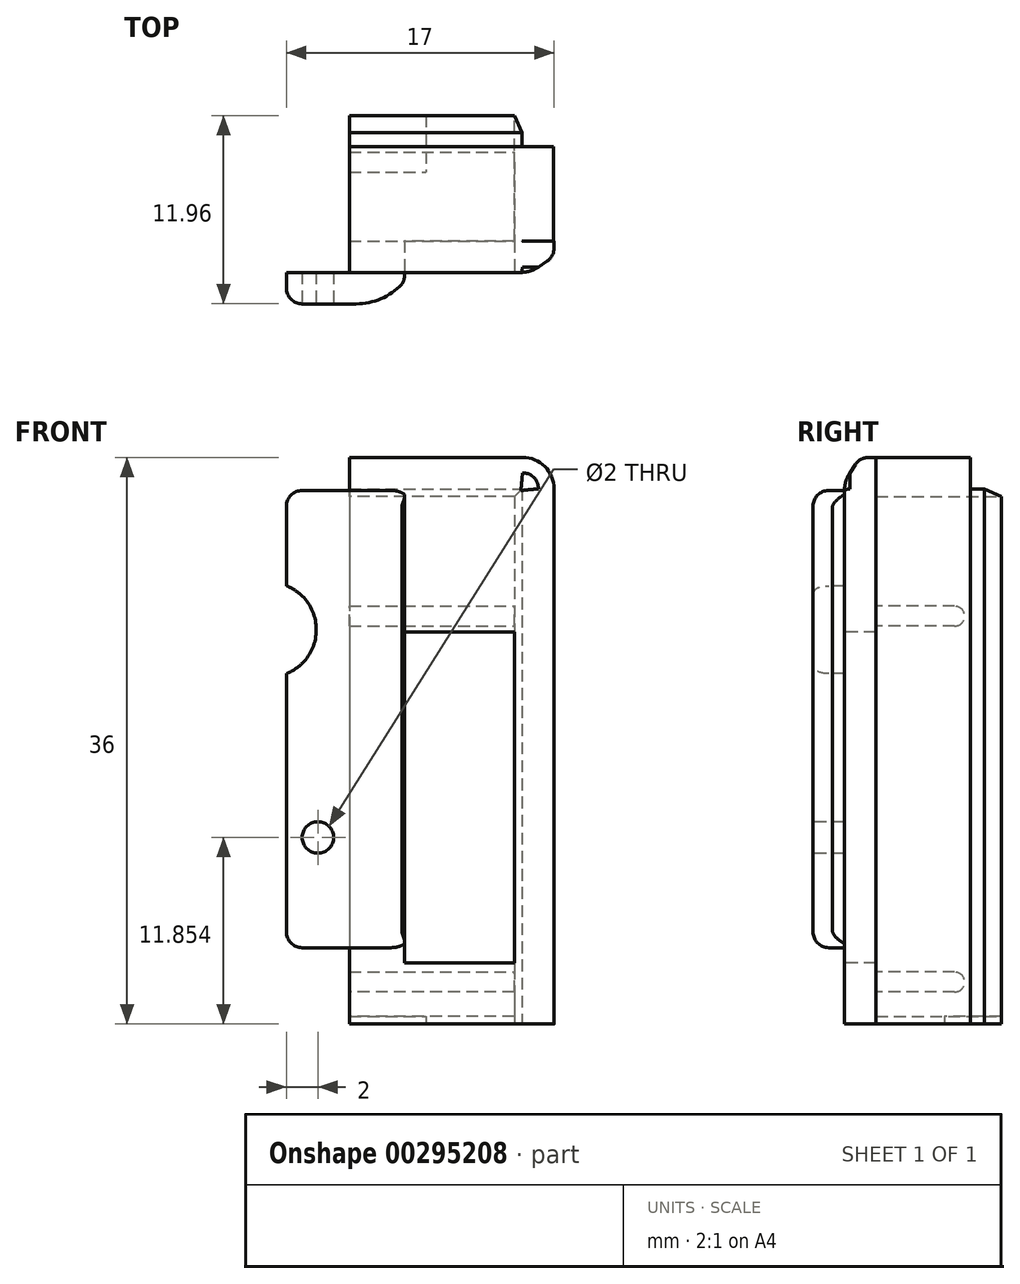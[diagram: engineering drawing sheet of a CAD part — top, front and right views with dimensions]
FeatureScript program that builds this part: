
annotation { "Feature Type Name" : "Feature", "Feature Type Description" : "" }
export const myFeature = defineFeature(function(context is Context, id is Id, definition is map)
    precondition{}
    {
        {
            var Q0;
            Q0=qCreatedBy(makeId("Front.planeOp"),FACE);
            var sketch = newSketch(context, id + "F0", { "sketchPlane" : qUnion([Q0])});
            skLineSegment(sketch, "E0", {"start": v(12.98, 36.3) * mm, "end": v(12.98, 70.29) * mm});
            skLineSegment(sketch, "E1", {"start": v(10.98, 72.29) * mm, "end": v(0, 72.29) * mm});
            skLineSegment(sketch, "E2", {"start": v(0, 72.29) * mm, "end": v(0, 70.29) * mm});
            skLineSegment(sketch, "E3", {"start": v(0, 70.29) * mm, "end": v(10.98, 70.29) * mm});
            skLineSegment(sketch, "E4", {"start": v(10.98, 70.29) * mm, "end": v(10.98, 36.3) * mm});
            skPoint(sketch, "E5.visualSharp", {"position": v(12.98, 72.29) * mm});
            skArc(sketch, "E5.filletArc", {"start": v(12.98, 70.29) * mm, "mid": v(12.4, 71.7) * mm, "end": v(10.98, 72.29) * mm});
            skPoint(sketch, "E6.visualSharp", {"position": v(12.98, 0) * mm});
            skLineSegment(sketch, "E7", {"start": v(10.98, 36.3) * mm, "end": v(12.98, 36.3) * mm});
            skPoint(sketch, "E8.start.orphan", {"position": v(0, 2) * mm});
            skSolve(sketch);
        }
        {
            var Q0;
            Q0=makeQuery(id+"F0.imprint","IMPRINT",FACE,{"disambiguationData":[TD([[makeQuery(id+"F0.imprint","IMPRINT",EDGE,{"derivedFrom":sQuery(id+"F0.wireOp",EDGE,"E0")}),1.0]])]});
            extrude(context, id + "F1", {"entities" : qUnion([Q0]), "depth" : 6 * mm});
        }
        {
            var Q0;
            Q0=makeQuery(id+"F1.opExtrude","SWEPT_FACE",FACE,{"disambiguationData":[OSD([sQuery(id+"F0.wireOp",EDGE,"E2")])]});
            var sketch = newSketch(context, id + "F2", { "sketchPlane" : qUnion([Q0])});
            skLineSegment(sketch, "E9.bottom", {"start": v(6, 72.29) * mm, "end": v(8, 72.29) * mm});
            skLineSegment(sketch, "E9.top", {"start": v(6, 36.3) * mm, "end": v(8, 36.3) * mm});
            skLineSegment(sketch, "E9.left", {"start": v(6, 72.29) * mm, "end": v(6, 36.3) * mm});
            skLineSegment(sketch, "E9.right", {"start": v(8, 72.29) * mm, "end": v(8, 36.3) * mm});
            skSolve(sketch);
        }
        {
            var Q0;
            Q0 = qSketchRegion(id + "F2", true);
            extrude(context, id + "F3", {"entities" : qUnion([Q0]), "operationType" : NewBodyOperationType.ADD, "oppositeDirection" : true, "depth" : 13 * mm});
        }
        {
            var Q0;
            Q0=makeQuery(id+"F3.opExtrude","CAP_EDGE",EDGE,{"disambiguationData":[OSD([sQuery(id+"F2.wireOp",EDGE,"E9.bottom")])],"isStart":false});
            fillet(context, id + "F4", {"entities" : qUnion([Q0]), "radius" : 2 * mm, "tangentPropagation" : true, "allowEdgeOverflow" : false});
        }
        {
            var Q0;
            Q0=makeQuery(id+"F3.opExtrude","SWEPT_FACE",FACE,{"disambiguationData":[OSD([sQuery(id+"F2.wireOp",EDGE,"E9.right")])]});
            var sketch = newSketch(context, id + "F5", { "sketchPlane" : qUnion([Q0])});
            skLineSegment(sketch, "E10.bottom", {"start": v(3.5, 70.18) * mm, "end": v(-4, 70.18) * mm});
            skLineSegment(sketch, "E10.top", {"start": v(3.5, 41.14) * mm, "end": v(-4, 41.14) * mm});
            skLineSegment(sketch, "E10.left", {"start": v(3.5, 70.18) * mm, "end": v(3.5, 41.14) * mm});
            skLineSegment(sketch, "E10.right", {"start": v(-4, 70.18) * mm, "end": v(-4, 41.14) * mm});
            skSolve(sketch);
        }
        {
            var Q0;
            Q0 = qSketchRegion(id + "F5", true);
            extrude(context, id + "F6", {"entities" : qUnion([Q0]), "operationType" : NewBodyOperationType.ADD, "depth" : 2 * mm});
        }
        {
            var Q0;
            Q0=makeQuery(id+"F6.opExtrude","CAP_EDGE",EDGE,{"disambiguationData":[OSD([sQuery(id+"F5.wireOp",EDGE,"E10.left")])],"isStart":false});
            chamfer(context, id + "F7", {"entities" : qUnion([Q0]), "chamferType" : ChamferType.TWO_OFFSETS, "width1" : 1.5 * mm, "oppositeDirection" : false, "width2" : 1 * mm, "tangentPropagation" : true});
        }
        {
            var Q0;
            {var subQ0=sQuery(id+"F5.wireOp",EDGE,"E10.left");Q0=makeQuery(id+"F7.opChamfer","BLEND_EDGE",EDGE,{"blendedFrom":[makeQuery(id+"F6.opExtrude","CAP_EDGE",EDGE,{"disambiguationData":[OSD([subQ0])],"isStart":false}),makeQuery(id+"F6.opExtrude","SWEPT_FACE",FACE,{"disambiguationData":[OSD([subQ0])]})],"blendedInto":[makeQuery(id+"F6.opExtrude","SWEPT_FACE",FACE,{"disambiguationData":[OSD([subQ0])]})]});}
            fillet(context, id + "F8", {"entities" : qUnion([Q0]), "radius" : 1 * mm, "tangentPropagation" : true, "allowEdgeOverflow" : false});
        }
        {
            var Q0;
            Q0=makeQuery(id+"F6.opExtrude","CAP_FACE",FACE,{"disambiguationData":[OSD([sQuery(id+"F5.wireOp",EDGE,"E10.bottom"),sQuery(id+"F5.wireOp",EDGE,"E10.top"),sQuery(id+"F5.wireOp",EDGE,"E10.left"),sQuery(id+"F5.wireOp",EDGE,"E10.right")])],"isStart":false});
            var sketch = newSketch(context, id + "F9", { "sketchPlane" : qUnion([Q0])});
            skCircle(sketch, "E11", {"center": v(-2, 48.14) * mm, "radius": 1 * mm});
            skSolve(sketch);
        }
        {
            var Q0;
            Q0 = qSketchRegion(id + "F9", true);
            extrude(context, id + "F10", {"entities" : qUnion([Q0]), "operationType" : NewBodyOperationType.REMOVE, "oppositeDirection" : true, "depth" : 25 * mm});
        }
        {
            var Q0;
            Q0=makeQuery(id+"F3.opExtrude","SWEPT_EDGE",EDGE,{"disambiguationData":[OSD([sQuery(id+"F2.wireOp",EDGE,"E9.bottom"),sQuery(id+"F2.wireOp",EDGE,"E9.right")])]});
            chamfer(context, id + "F11", {"entities" : qUnion([Q0]), "chamferType" : ChamferType.TWO_OFFSETS, "width1" : 1.5 * mm, "oppositeDirection" : false, "width2" : 1 * mm, "tangentPropagation" : true});
        }
        {
            var Q0;
            {var subQ0=sQuery(id+"F2.wireOp",EDGE,"E9.bottom");Q0=makeQuery(id+"F11.opChamfer","BLEND_EDGE",EDGE,{"blendedFrom":[makeQuery(id+"F3.opExtrude","SWEPT_EDGE",EDGE,{"disambiguationData":[OSD([subQ0,sQuery(id+"F2.wireOp",EDGE,"E9.right")])]}),makeQuery(id+"F3.boolean.opBoolean","MERGE",FACE,{"derivedFrom":[makeQuery(id+"F1.opExtrude","SWEPT_FACE",FACE,{"disambiguationData":[OSD([sQuery(id+"F0.wireOp",EDGE,"E1")])]}),makeQuery(id+"F3.opExtrude","SWEPT_FACE",FACE,{"disambiguationData":[OSD([subQ0])]})]})],"blendedInto":[makeQuery(id+"F3.boolean.opBoolean","MERGE",FACE,{"derivedFrom":[makeQuery(id+"F1.opExtrude","SWEPT_FACE",FACE,{"disambiguationData":[OSD([sQuery(id+"F0.wireOp",EDGE,"E1")])]}),makeQuery(id+"F3.opExtrude","SWEPT_FACE",FACE,{"disambiguationData":[OSD([subQ0])]})]})]});}
            fillet(context, id + "F12", {"entities" : qUnion([Q0]), "radius" : 1 * mm, "tangentPropagation" : true, "allowEdgeOverflow" : false});
        }
        {
            var Q0;
            {var subQ0=sQuery(id+"F2.wireOp",EDGE,"E9.right");Q0=makeQuery(id+"F11.opChamfer","BLEND_EDGE",EDGE,{"blendedFrom":[makeQuery(id+"F3.opExtrude","SWEPT_EDGE",EDGE,{"disambiguationData":[OSD([sQuery(id+"F2.wireOp",EDGE,"E9.bottom"),subQ0])]}),makeQuery(id+"F3.opExtrude","SWEPT_FACE",FACE,{"disambiguationData":[OSD([subQ0])]})],"blendedInto":[makeQuery(id+"F3.opExtrude","SWEPT_FACE",FACE,{"disambiguationData":[OSD([subQ0])]})]});}
            fillet(context, id + "F13", {"entities" : qUnion([Q0]), "radius" : 2 * mm, "tangentPropagation" : true, "allowEdgeOverflow" : false});
        }
        {
            var Q0;
            {var subQ0=sQuery(id+"F5.wireOp",EDGE,"E10.left");Q0=makeQuery(id+"F7.opChamfer","BLEND_EDGE",EDGE,{"blendedFrom":[makeQuery(id+"F6.opExtrude","CAP_EDGE",EDGE,{"disambiguationData":[OSD([subQ0])],"isStart":false}),makeQuery(id+"F6.opExtrude","CAP_FACE",FACE,{"disambiguationData":[OSD([sQuery(id+"F5.wireOp",EDGE,"E10.bottom"),sQuery(id+"F5.wireOp",EDGE,"E10.top"),subQ0,sQuery(id+"F5.wireOp",EDGE,"E10.right")])],"isStart":false})],"blendedInto":[makeQuery(id+"F6.opExtrude","CAP_FACE",FACE,{"disambiguationData":[OSD([sQuery(id+"F5.wireOp",EDGE,"E10.bottom"),sQuery(id+"F5.wireOp",EDGE,"E10.top"),subQ0,sQuery(id+"F5.wireOp",EDGE,"E10.right")])],"isStart":false})]});}
            fillet(context, id + "F14", {"entities" : qUnion([Q0]), "radius" : 4 * mm, "tangentPropagation" : true, "allowEdgeOverflow" : false});
        }
        {
            var Q0;
            Q0=makeQuery(id+"F6.opExtrude","CAP_EDGE",EDGE,{"disambiguationData":[OSD([sQuery(id+"F5.wireOp",EDGE,"E10.top")])],"isStart":false});
            var Q1;
            Q1=makeQuery(id+"F6.opExtrude","CAP_EDGE",EDGE,{"disambiguationData":[OSD([sQuery(id+"F5.wireOp",EDGE,"E10.bottom")])],"isStart":false});
            fillet(context, id + "F15", {"entities" : qUnion([Q0, Q1]), "radius" : 1 * mm, "tangentPropagation" : true, "allowEdgeOverflow" : false});
        }
        {
            var Q0;
            Q0=makeQuery(id+"F6.opExtrude","CAP_EDGE",EDGE,{"disambiguationData":[OSD([sQuery(id+"F5.wireOp",EDGE,"E10.right")])],"isStart":false});
            fillet(context, id + "F16", {"entities" : qUnion([Q0]), "radius" : 1 * mm, "tangentPropagation" : true, "allowEdgeOverflow" : false});
        }
        {
            var Q0;
            Q0=makeQuery(id+"F1.opExtrude","CAP_FACE",FACE,{"disambiguationData":[OSD([sQuery(id+"F0.wireOp",EDGE,"E0"),sQuery(id+"F0.wireOp",EDGE,"E1"),sQuery(id+"F0.wireOp",EDGE,"E2"),sQuery(id+"F0.wireOp",EDGE,"E3"),sQuery(id+"F0.wireOp",EDGE,"E4"),sQuery(id+"F0.wireOp",EDGE,"E5.filletArc"),sQuery(id+"F0.wireOp",EDGE,"E7")])],"isStart":true});
            var sketch = newSketch(context, id + "F17", { "sketchPlane" : qUnion([Q0])});
            skLineSegment(sketch, "E12.bottom", {"start": v(-10.98, 70.29) * mm, "end": v(-10.48, 70.29) * mm});
            skLineSegment(sketch, "E12.top", {"start": v(-10.98, 36.3) * mm, "end": v(-10.48, 36.3) * mm});
            skLineSegment(sketch, "E12.left", {"start": v(-10.98, 70.29) * mm, "end": v(-10.98, 36.3) * mm});
            skLineSegment(sketch, "E12.right", {"start": v(-10.48, 70.29) * mm, "end": v(-10.48, 36.3) * mm});
            skLineSegment(sketch, "E13.bottom", {"start": v(-10.98, 70.29) * mm, "end": v(0, 70.29) * mm});
            skLineSegment(sketch, "E13.top", {"start": v(-10.98, 69.79) * mm, "end": v(0, 69.79) * mm});
            skLineSegment(sketch, "E13.left", {"start": v(-10.98, 70.29) * mm, "end": v(-10.98, 69.79) * mm});
            skLineSegment(sketch, "E13.right", {"start": v(0, 70.29) * mm, "end": v(0, 69.79) * mm});
            skLineSegment(sketch, "E14.bottom", {"start": v(-10.98, 36.3) * mm, "end": v(0, 36.3) * mm});
            skLineSegment(sketch, "E14.top", {"start": v(-10.98, 36.8) * mm, "end": v(0, 36.8) * mm});
            skLineSegment(sketch, "E14.left", {"start": v(-10.98, 36.3) * mm, "end": v(-10.98, 36.8) * mm});
            skLineSegment(sketch, "E14.right", {"start": v(0, 36.3) * mm, "end": v(0, 36.8) * mm});
            skSolve(sketch);
        }
        {
            var Q0;
            Q0 = qSketchRegion(id + "F17", true);
            extrude(context, id + "F18", {"entities" : qUnion([Q0]), "operationType" : NewBodyOperationType.ADD, "oppositeDirection" : true, "depth" : 6.1 * mm, "hasSecondDirection" : true, "secondDirectionOppositeDirection" : false, "secondDirectionDepth" : 1.97 * mm});
        }
        {
            var Q0;
            Q0=makeQuery(id+"F18.opExtrude","CAP_EDGE",EDGE,{"disambiguationData":[OSD([sQuery(id+"F17.wireOp",EDGE,"E12.left"),sQuery(id+"F17.wireOp",EDGE,"E13.left")])],"isStart":true});
            var Q1;
            Q1=makeQuery(id+"F18.opExtrude","CAP_EDGE",EDGE,{"disambiguationData":[OSD([sQuery(id+"F17.wireOp",EDGE,"E13.bottom")])],"isStart":true});
            chamfer(context, id + "F19", {"entities" : qUnion([Q0, Q1]), "chamferType" : ChamferType.OFFSET_ANGLE, "width" : 0.5 * mm, "oppositeDirection" : false, "angle" : 65 * degree, "tangentPropagation" : true});
        }
        {
            var Q0;
            Q0=makeQuery(id+"F18.boolean.opBoolean","MERGE",FACE,{"derivedFrom":[makeQuery(id+"F3.boolean.opBoolean","MERGE",FACE,{"derivedFrom":[makeQuery(id+"F1.opExtrude","SWEPT_FACE",FACE,{"disambiguationData":[OSD([sQuery(id+"F0.wireOp",EDGE,"E7")])]}),makeQuery(id+"F3.opExtrude","SWEPT_FACE",FACE,{"disambiguationData":[OSD([sQuery(id+"F2.wireOp",EDGE,"E9.top")])]})]}),makeQuery(id+"F18.opExtrude","SWEPT_FACE",FACE,{"disambiguationData":[OSD([sQuery(id+"F17.wireOp",EDGE,"E14.bottom")])]})]});
            var sketch = newSketch(context, id + "F20", { "sketchPlane" : qUnion([Q0])});
            skLineSegment(sketch, "E15.bottom", {"start": v(0, -1.97) * mm, "end": v(4.88, -1.97) * mm});
            skLineSegment(sketch, "E15.top", {"start": v(0, 1.64) * mm, "end": v(4.88, 1.64) * mm});
            skLineSegment(sketch, "E15.left", {"start": v(0, -1.97) * mm, "end": v(0, 1.64) * mm});
            skLineSegment(sketch, "E15.right", {"start": v(4.88, -1.97) * mm, "end": v(4.88, 1.64) * mm});
            skSolve(sketch);
        }
        {
            var Q0;
            Q0=makeQuery(id+"F20.imprint","IMPRINT",FACE,{"disambiguationData":[TD([[makeQuery(id+"F20.imprint","IMPRINT",EDGE,{"derivedFrom":sQuery(id+"F20.wireOp",EDGE,"E15.bottom")}),-1.0]])]});
            extrude(context, id + "F21", {"entities" : qUnion([Q0]), "operationType" : NewBodyOperationType.REMOVE, "oppositeDirection" : true, "depth" : 3.3 * mm});
        }
        {
            var Q0;
            {var subQ1=sQuery(id+"F2.wireOp",EDGE,"E9.left");Q0=makeQuery(id+"F3.boolean.opBoolean","SPLIT",FACE,{"disambiguationData":[TD([makeQuery(id+"F1.opExtrude","SWEPT_FACE",FACE,{"disambiguationData":[OSD([sQuery(id+"F0.wireOp",EDGE,"E2")])]})])],"derivedFrom":makeQuery(id+"F3.opExtrude","SWEPT_FACE",FACE,{"disambiguationData":[OSD([subQ1])]})});}
            var sketch = newSketch(context, id + "F22", { "sketchPlane" : qUnion([Q0])});
            skLineSegment(sketch, "E16", {"start": v(-10.48, 38.33) * mm, "end": v(-7.39, 38.33) * mm});
            skLineSegment(sketch, "E17", {"start": v(-10.48, 39.6) * mm, "end": v(-7.39, 39.6) * mm});
            skLineSegment(sketch, "E18", {"start": v(-7.39, 38.33) * mm, "end": v(0, 38.33) * mm});
            skLineSegment(sketch, "E19", {"start": v(0, 38.33) * mm, "end": v(0, 39.6) * mm});
            skLineSegment(sketch, "E20", {"start": v(0, 39.6) * mm, "end": v(-7.39, 39.6) * mm});
            skLineSegment(sketch, "E21.bottom", {"start": v(0, 62.84) * mm, "end": v(-10.48, 62.84) * mm});
            skLineSegment(sketch, "E21.top", {"start": v(0, 61.57) * mm, "end": v(-10.48, 61.57) * mm});
            skLineSegment(sketch, "E21.left", {"start": v(0, 62.84) * mm, "end": v(0, 61.57) * mm});
            skLineSegment(sketch, "E21.right", {"start": v(-10.48, 62.84) * mm, "end": v(-10.48, 61.57) * mm});
            skSolve(sketch);
        }
        {
            var Q0;
            {var subQ0=sQuery(id+"F22.wireOp",EDGE,"E16");Q0=makeQuery(id+"F22.imprint","IMPRINT",FACE,{"disambiguationData":[TD([[makeQuery(id+"F22.imprint","IMPRINT",EDGE,{"derivedFrom":subQ0}),1.0]])]});}
            var Q1;
            Q1=makeQuery(id+"F22.imprint","IMPRINT",FACE,{"disambiguationData":[TD([[makeQuery(id+"F22.imprint","IMPRINT",EDGE,{"derivedFrom":sQuery(id+"F22.wireOp",EDGE,"E21.bottom")}),1.0]])]});
            extrude(context, id + "F23", {"entities" : qUnion([Q0, Q1]), "operationType" : NewBodyOperationType.ADD, "depth" : 5.63 * mm});
        }
        {
            var Q0;
            Q0=makeQuery(id+"F23.opExtrude","CAP_EDGE",EDGE,{"disambiguationData":[OSD([sQuery(id+"F22.wireOp",EDGE,"E16")])],"isStart":false});
            var Q1;
            Q1=makeQuery(id+"F23.opExtrude","CAP_EDGE",EDGE,{"disambiguationData":[OSD([sQuery(id+"F22.wireOp",EDGE,"E17")])],"isStart":false});
            var Q2;
            Q2=makeQuery(id+"F23.opExtrude","CAP_EDGE",EDGE,{"disambiguationData":[OSD([sQuery(id+"F22.wireOp",EDGE,"E21.top")])],"isStart":false});
            var Q3;
            Q3=makeQuery(id+"F23.opExtrude","CAP_EDGE",EDGE,{"disambiguationData":[OSD([sQuery(id+"F22.wireOp",EDGE,"E21.bottom")])],"isStart":false});
            fillet(context, id + "F24", {"entities" : qUnion([Q0, Q1, Q2, Q3]), "radius" : 0.64 * mm, "tangentPropagation" : true, "allowEdgeOverflow" : false});
        }
        {
            var Q0;
            Q0=makeQuery(id+"F3.opExtrude","SWEPT_FACE",FACE,{"disambiguationData":[OSD([sQuery(id+"F2.wireOp",EDGE,"E9.right")])]});
            var sketch = newSketch(context, id + "F25", { "sketchPlane" : qUnion([Q0])});
            skLineSegment(sketch, "E22.bottom", {"start": v(3.5, 61.18) * mm, "end": v(10.48, 61.18) * mm});
            skLineSegment(sketch, "E22.top", {"start": v(3.5, 40.18) * mm, "end": v(10.48, 40.18) * mm});
            skLineSegment(sketch, "E22.left", {"start": v(3.5, 61.18) * mm, "end": v(3.5, 40.18) * mm});
            skLineSegment(sketch, "E22.right", {"start": v(10.48, 61.18) * mm, "end": v(10.48, 40.18) * mm});
            skSolve(sketch);
        }
        {
            var Q0;
            Q0=makeQuery(id+"F25.imprint","IMPRINT",FACE,{"disambiguationData":[TD([[makeQuery(id+"F25.imprint","IMPRINT",EDGE,{"derivedFrom":sQuery(id+"F25.wireOp",EDGE,"E22.bottom")}),-1.0]])]});
            extrude(context, id + "F26", {"entities" : qUnion([Q0]), "operationType" : NewBodyOperationType.REMOVE, "oppositeDirection" : true, "depth" : 25 * mm});
        }
        {
            var Q0;
            Q0=makeQuery(id+"F16.opFillet","SPLIT",FACE,{"disambiguationData":[OD(1.0)],"derivedFrom":makeQuery(id+"F6.opExtrude","CAP_FACE",FACE,{"disambiguationData":[OSD([sQuery(id+"F5.wireOp",EDGE,"E10.bottom"),sQuery(id+"F5.wireOp",EDGE,"E10.top"),sQuery(id+"F5.wireOp",EDGE,"E10.left"),sQuery(id+"F5.wireOp",EDGE,"E10.right")])],"isStart":false})});
            var sketch = newSketch(context, id + "F27", { "sketchPlane" : qUnion([Q0])});
            skCircle(sketch, "E23", {"center": v(-5.1, 61.34) * mm, "radius": 3 * mm});
            skSolve(sketch);
        }
        {
            var Q0;
            Q0 = qSketchRegion(id + "F27", true);
            extrude(context, id + "F28", {"entities" : qUnion([Q0]), "operationType" : NewBodyOperationType.REMOVE, "oppositeDirection" : true, "depth" : 25 * mm});
        }
    });
